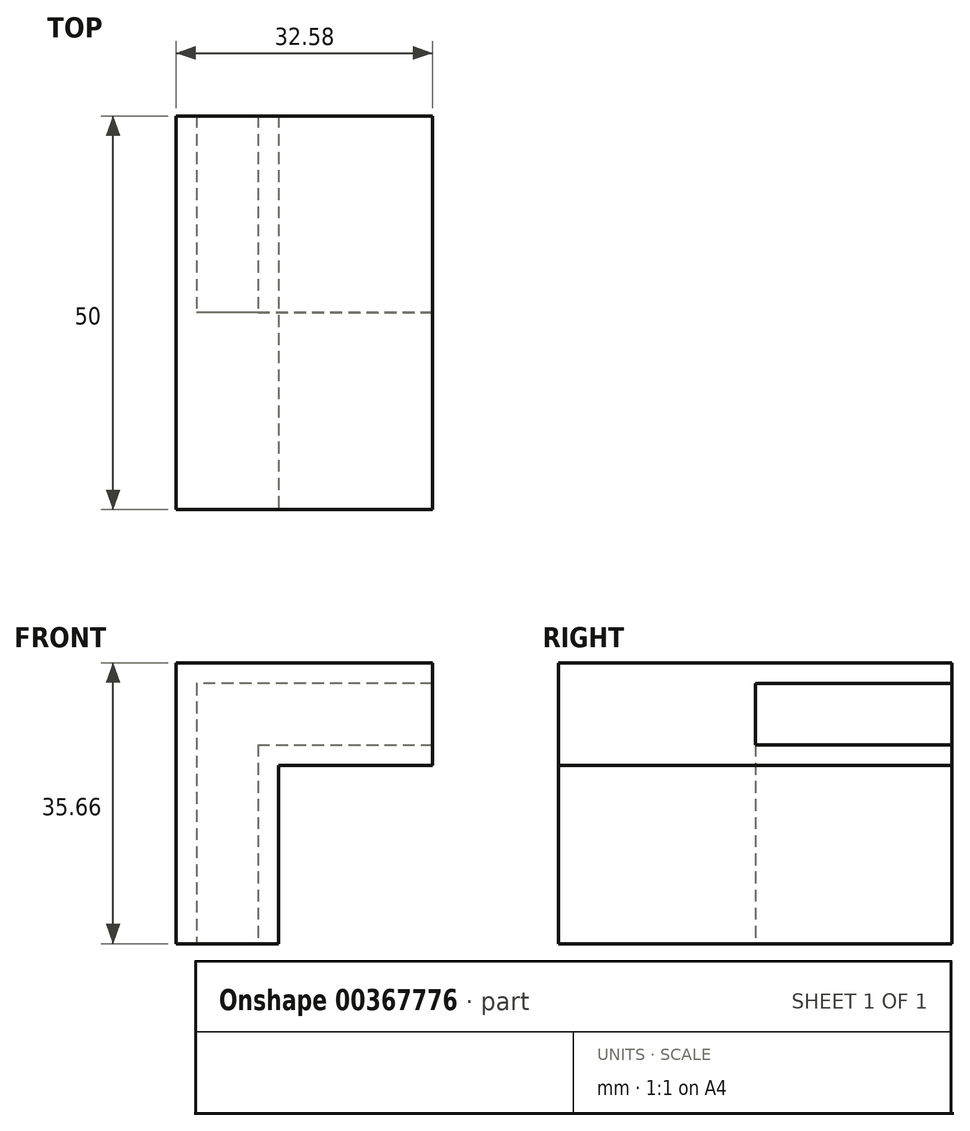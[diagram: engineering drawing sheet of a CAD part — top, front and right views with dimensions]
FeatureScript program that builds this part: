
annotation { "Feature Type Name" : "Feature", "Feature Type Description" : "" }
export const myFeature = defineFeature(function(context is Context, id is Id, definition is map)
    precondition{}
    {
        {
            var Q0;
            Q0=qCreatedBy(makeId("Front.planeOp"),FACE);
            var sketch = newSketch(context, id + "F0", { "sketchPlane" : qUnion([Q0])});
            skLineSegment(sketch, "E0.top", {"start": v(0, -22.66) * mm, "end": v(-13, -22.66) * mm});
            skLineSegment(sketch, "E0.left", {"start": v(0, 0) * mm, "end": v(0, -22.66) * mm});
            skLineSegment(sketch, "E0.right", {"start": v(-13, 0) * mm, "end": v(-13, -22.66) * mm});
            skLineSegment(sketch, "E1.bottom", {"start": v(0, 0) * mm, "end": v(19.58, 0) * mm});
            skLineSegment(sketch, "E1.top", {"start": v(0, 13) * mm, "end": v(19.58, 13) * mm});
            skLineSegment(sketch, "E1.right", {"start": v(19.58, 0) * mm, "end": v(19.58, 13) * mm});
            skLineSegment(sketch, "E2.top", {"start": v(0, 13) * mm, "end": v(-13, 13) * mm});
            skLineSegment(sketch, "E2.right", {"start": v(-13, 0) * mm, "end": v(-13, 13) * mm});
            skLineSegment(sketch, "E3.0", {"start": v(-10.4, 0) * mm, "end": v(-10.4, -22.66) * mm});
            skLineSegment(sketch, "E3.1", {"start": v(-10.4, 0) * mm, "end": v(-10.4, 10.4) * mm});
            skLineSegment(sketch, "E3.2", {"start": v(0, 10.4) * mm, "end": v(-10.4, 10.4) * mm});
            skLineSegment(sketch, "E3.3", {"start": v(0, 10.4) * mm, "end": v(19.58, 10.4) * mm});
            skLineSegment(sketch, "E4.0", {"start": v(-2.6, 2.6) * mm, "end": v(-2.6, -22.66) * mm});
            skLineSegment(sketch, "E4.1", {"start": v(-2.6, 2.6) * mm, "end": v(19.58, 2.6) * mm});
            skSolve(sketch);
        }
        {
            var Q0;
            {var subQ3=sQuery(id+"F0.wireOp",EDGE,"E0.right");Q0=makeQuery(id+"F0.imprint","IMPRINT",FACE,{"disambiguationData":[TD([[makeQuery(id+"F0.imprint","IMPRINT",EDGE,{"derivedFrom":subQ3}),1.0]])]});}
            var Q1;
            {var subQ3=sQuery(id+"F0.wireOp",EDGE,"E0.left");Q1=makeQuery(id+"F0.imprint","IMPRINT",FACE,{"disambiguationData":[TD([[makeQuery(id+"F0.imprint","IMPRINT",EDGE,{"derivedFrom":subQ3}),-1.0]])]});}
            extrude(context, id + "F1", {"entities" : qUnion([Q0, Q1]), "depth" : -25 * mm});
        }
        {
            var Q0;
            Q0=makeQuery(id+"F1.opExtrude","CAP_FACE",FACE,{"disambiguationData":[OSD([sQuery(id+"F0.wireOp",EDGE,"E0.top"),sQuery(id+"F0.wireOp",EDGE,"E0.left"),sQuery(id+"F0.wireOp",EDGE,"E1.bottom"),sQuery(id+"F0.wireOp",EDGE,"E1.right"),sQuery(id+"F0.wireOp",EDGE,"E4.0"),sQuery(id+"F0.wireOp",EDGE,"E4.1")])],"isStart":false});
            var Q1;
            Q1=makeQuery(id+"F1.opExtrude","CAP_FACE",FACE,{"disambiguationData":[OSD([sQuery(id+"F0.wireOp",EDGE,"E0.top"),sQuery(id+"F0.wireOp",EDGE,"E0.right"),sQuery(id+"F0.wireOp",EDGE,"E1.top"),sQuery(id+"F0.wireOp",EDGE,"E1.right"),sQuery(id+"F0.wireOp",EDGE,"E2.top"),sQuery(id+"F0.wireOp",EDGE,"E2.right"),sQuery(id+"F0.wireOp",EDGE,"E3.0"),sQuery(id+"F0.wireOp",EDGE,"E3.1"),sQuery(id+"F0.wireOp",EDGE,"E3.2"),sQuery(id+"F0.wireOp",EDGE,"E3.3")])],"isStart":false});
            var Q2;
            Q2 = qSketchRegion(id + "F0", true);
            extrude(context, id + "F2", {"entities" : qUnion([Q0, Q1, Q2]), "operationType" : NewBodyOperationType.ADD, "depth" : 25 * mm});
        }
    });
